# Revit family: Bath-Drop_In-BubbleMassage-Heated_Surface-KOHLER-Archer-K-1124_1
name_source: partatom
category: Plumbing Fixtures
units: mm (PartAtom-declared; Revit-internal decimal feet)

## family parameters
Cut with Voids When Loaded = No
Host = Face
OmniClass Number = 23.31.15.00
OmniClass Title = Bathtubs
Part Type = Normal
Room Calculation Point = No
Round Connector Dimension = Use Diameter
Shared = No

## types (6) — shared parameters
ADA Compliant = No
Amplifier Electrical Connector = Amplifier Electrical Connector
Apparent Load = 1800 VA
Assembly Code = D2010500
Blower Electrical Connector = Blower Electrical Connector
CW Connection = No
Cold Water Inlet = Cold Water Inlet
Date Modified = 03/08/2023
Default Elevation = 0"
Description = 72 Inch x 36 Inch heated Bubble Massage air bath with Bask, reversible drain
Drain Included = No
Electrical Connector = Yes
Electrical Note = Two dedicated circuits required, protected with Class A GroundFault Circuit-Interrupter (GFCI). Outside North America, this device may be known as a Residual Current Device (RCD).
HW Connection = No
Heater Electrical Connector = Heater Electrical Connector
Height = 19"
Hot Water Inlet = Hot Water Inlet
Length = 72"
Manufacturer = Kohler Co.
Master Format 2014 = 22 41 19
Master Format 2014 Name = Residential Bathtubs
Material = Acrylic
Product Documentation Link = https://www.us.kohler.com
Product Name = Archer
Product Page URL = http://www.us.kohler.com
Pump Electrical Connector = Pump Electrical Connector
URL = https://www.us.kohler.com
Vent Connection = No
Voltage = 120 V
Waste Connection = Yes
Waste Water Outlet = Waste Water Outlet
WaterSense Certified = No
Width = 36"

## per-type parameters (varying)
| type | Finish | Model | Type |
| 0-White | Kohler-Acrylic-0-White | K-1124-GHW-0 | 1 |
| 7-Black Black | KOHLER-Acrylic-7-Black_Black | K-1124-GHW-7 | 2 |
| 58-Thunder Grey | KOHLER-Acrylic-58-Thunder_Grey | K-1124-GHW-58 | 3 |
| 95-Ice Grey | KOHLER-Acrylic-95-Ice_Grey | K-1124-GHW-95 | 4 |
| 96-Biscuit | KOHLER-Acrylic-96-Biscuit | K-1124-GHW-96 | 5 |
| NY-Dune | KOHLER-Acrylic-NY-Dune | K-1124-GHW-NY | 6 |

## geometry (parser evidence)
native form markers: Sweep x6
no freeform markers — native parametric forms only
